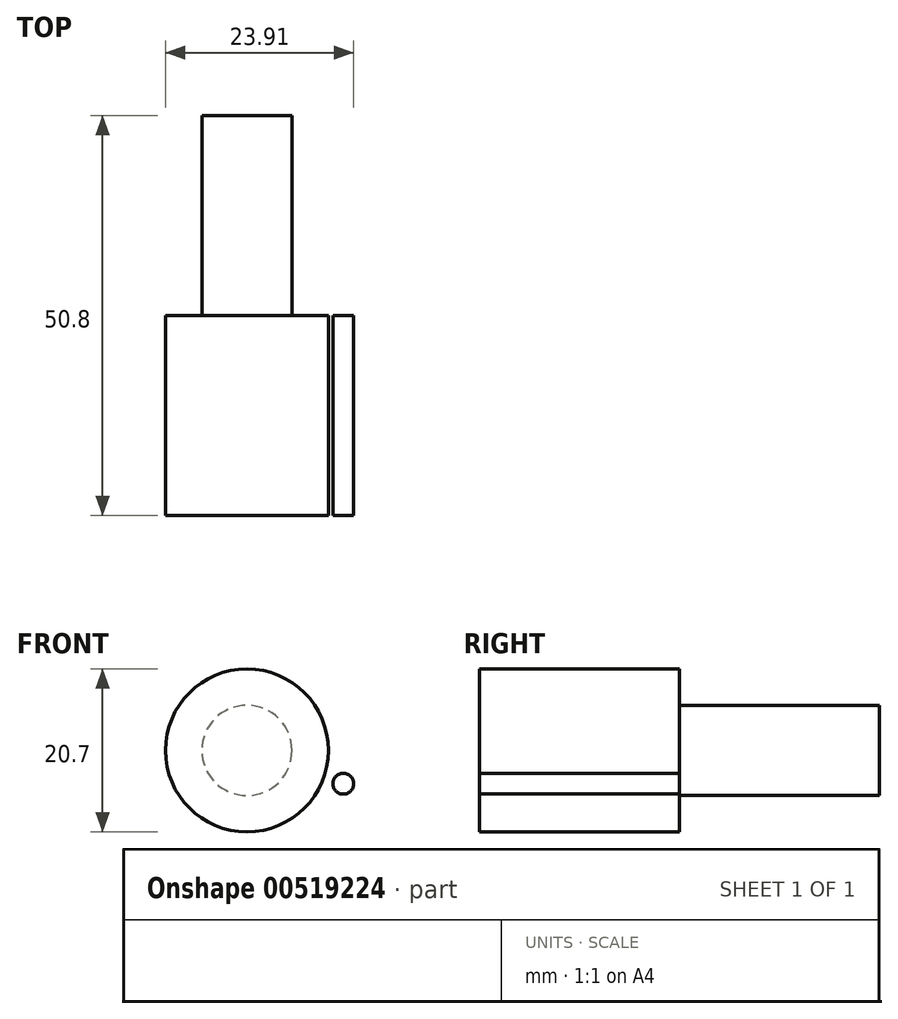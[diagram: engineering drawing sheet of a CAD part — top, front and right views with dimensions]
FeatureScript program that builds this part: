
annotation { "Feature Type Name" : "Feature", "Feature Type Description" : "" }
export const myFeature = defineFeature(function(context is Context, id is Id, definition is map)
    precondition{}
    {
        {
            var Q0;
            Q0=qCreatedBy(makeId("Front.planeOp"),FACE);
            var sketch = newSketch(context, id + "F0", { "sketchPlane" : qUnion([Q0])});
            skCircle(sketch, "E0", {"center": v(0, 0) * mm, "radius": 1.32 * mm});
            skCircle(sketch, "E1", {"center": v(-12.24, 4.23) * mm, "radius": 10.35 * mm});
            skSolve(sketch);
        }
        {
            var Q0;
            Q0 = qSketchRegion(id + "F0", true);
            extrude(context, id + "F1", {"entities" : qUnion([Q0]), "depth" : 25.4 * mm, "offsetDistance" : 25.4 * mm});
        }
        {
            var Q0;
            Q0=makeQuery(id+"F1.opExtrude","CAP_FACE",FACE,{"disambiguationData":[OSD([sQuery(id+"F0.wireOp",EDGE,"E1")])],"isStart":true});
            var sketch = newSketch(context, id + "F2", { "sketchPlane" : qUnion([Q0])});
            skCircle(sketch, "E2", {"center": v(12.24, 4.23) * mm, "radius": 5.73 * mm});
            skSolve(sketch);
        }
        {
            var Q0;
            Q0=makeQuery(id+"F2.imprint","IMPRINT",FACE,{"disambiguationData":[TD([[makeQuery(id+"F2.imprint","IMPRINT",EDGE,{"derivedFrom":sQuery(id+"F2.wireOp",EDGE,"E2")}),1.0]])]});
            extrude(context, id + "F3", {"entities" : qUnion([Q0]), "operationType" : NewBodyOperationType.ADD, "depth" : 25.4 * mm, "offsetDistance" : 25.4 * mm});
        }
    });
